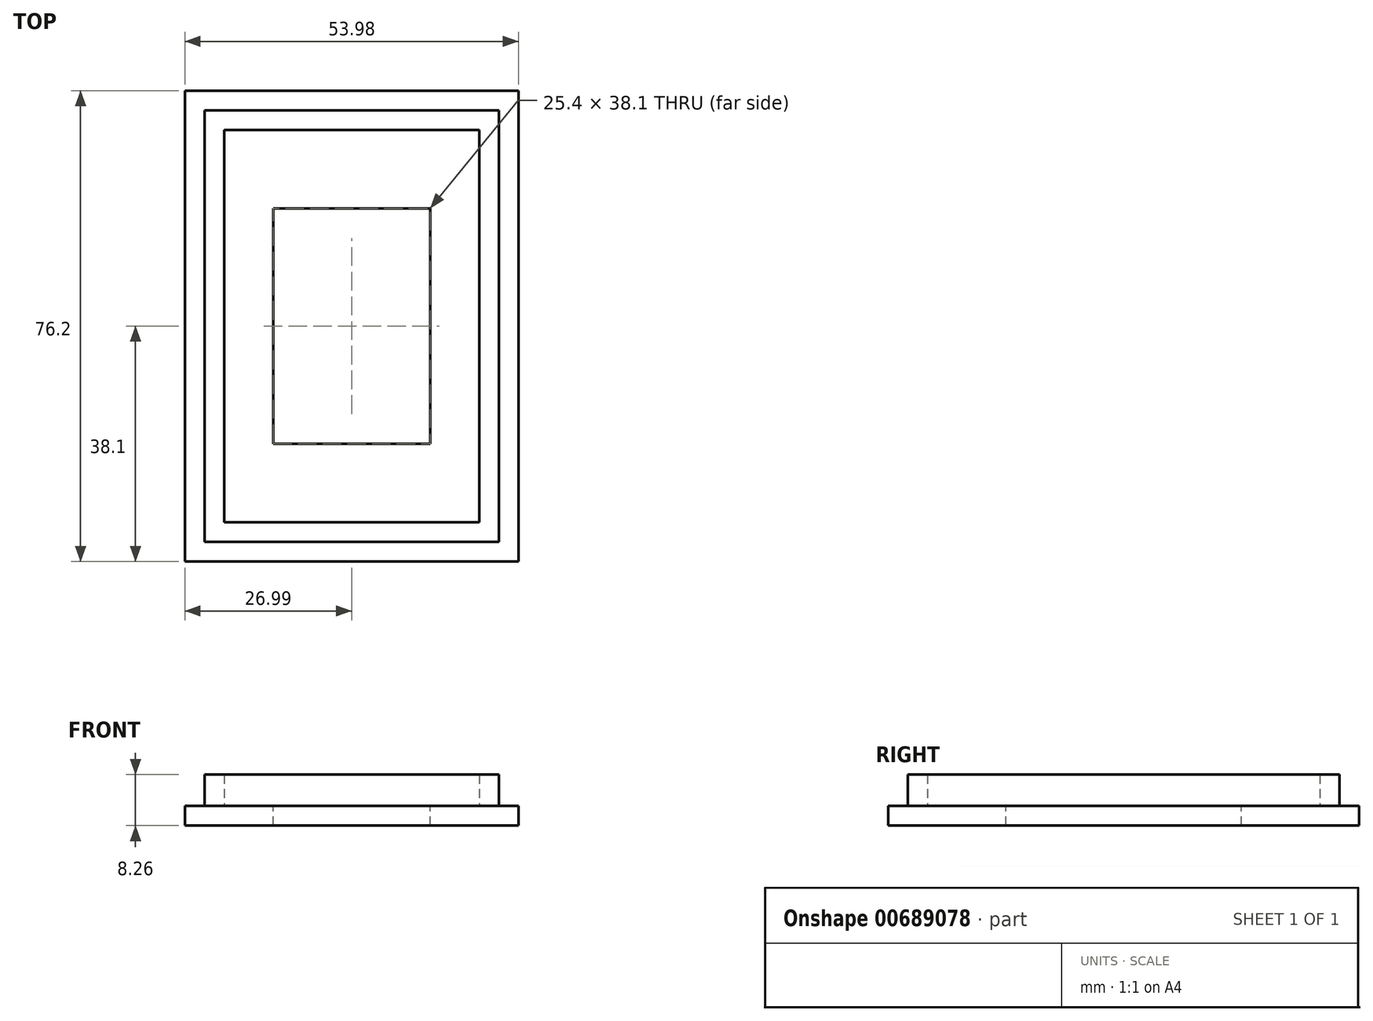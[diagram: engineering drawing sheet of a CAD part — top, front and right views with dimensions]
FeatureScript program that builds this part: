
annotation { "Feature Type Name" : "Feature", "Feature Type Description" : "" }
export const myFeature = defineFeature(function(context is Context, id is Id, definition is map)
    precondition{}
    {
        {
            var Q0;
            Q0=qCreatedBy(makeId("Top.planeOp"),FACE);
            var sketch = newSketch(context, id + "F0", { "sketchPlane" : qUnion([Q0])});
            skLineSegment(sketch, "E0.bottom", {"start": v(-26.99, 38.1) * mm, "end": v(26.99, 38.1) * mm});
            skLineSegment(sketch, "E0.top", {"start": v(-26.99, -38.1) * mm, "end": v(26.99, -38.1) * mm});
            skLineSegment(sketch, "E0.left", {"start": v(-26.99, 38.1) * mm, "end": v(-26.99, -38.1) * mm});
            skLineSegment(sketch, "E0.right", {"start": v(26.99, 38.1) * mm, "end": v(26.99, -38.1) * mm});
            skPoint(sketch, "E0.middle", {"position": v(0, 0) * mm});
            skSolve(sketch);
        }
        {
            var Q0;
            Q0=makeQuery(id+"F0.imprint","IMPRINT",FACE,{"disambiguationData":[TD([[makeQuery(id+"F0.imprint","IMPRINT",EDGE,{"derivedFrom":sQuery(id+"F0.wireOp",EDGE,"E0.bottom")}),-1.0]])]});
            extrude(context, id + "F1", {"entities" : qUnion([Q0]), "depth" : 3.17 * mm, "offsetDistance" : 25.4 * mm});
        }
        {
            var Q0;
            Q0=makeQuery(id+"F1.opExtrude","CAP_FACE",FACE,{"disambiguationData":[OSD([sQuery(id+"F0.wireOp",EDGE,"E0.bottom"),sQuery(id+"F0.wireOp",EDGE,"E0.top"),sQuery(id+"F0.wireOp",EDGE,"E0.left"),sQuery(id+"F0.wireOp",EDGE,"E0.right")])],"isStart":false});
            var sketch = newSketch(context, id + "F2", { "sketchPlane" : qUnion([Q0])});
            skLineSegment(sketch, "E1.bottom", {"start": v(-23.81, 34.93) * mm, "end": v(23.81, 34.93) * mm});
            skLineSegment(sketch, "E1.top", {"start": v(-23.81, -34.93) * mm, "end": v(23.81, -34.93) * mm});
            skLineSegment(sketch, "E1.left", {"start": v(-23.81, 34.93) * mm, "end": v(-23.81, -34.93) * mm});
            skLineSegment(sketch, "E1.right", {"start": v(23.81, 34.93) * mm, "end": v(23.81, -34.93) * mm});
            skPoint(sketch, "E1.middle", {"position": v(0, 0) * mm});
            skSolve(sketch);
        }
        {
            var Q0;
            Q0=makeQuery(id+"F2.imprint","IMPRINT",FACE,{"disambiguationData":[TD([[makeQuery(id+"F2.imprint","IMPRINT",EDGE,{"derivedFrom":sQuery(id+"F2.wireOp",EDGE,"E1.bottom")}),-1.0]])]});
            extrude(context, id + "F3", {"entities" : qUnion([Q0]), "operationType" : NewBodyOperationType.ADD, "depth" : 5.08 * mm, "offsetDistance" : 25.4 * mm});
        }
        {
            var Q0;
            Q0=makeQuery(id+"F3.opExtrude","CAP_FACE",FACE,{"disambiguationData":[OSD([sQuery(id+"F2.wireOp",EDGE,"E1.bottom"),sQuery(id+"F2.wireOp",EDGE,"E1.top"),sQuery(id+"F2.wireOp",EDGE,"E1.left"),sQuery(id+"F2.wireOp",EDGE,"E1.right")])],"isStart":false});
            shell(context, id + "F4", {"entities" : qUnion([Q0]), "thickness" : 3.17 * mm});
        }
        {
            var Q0;
            Q0=makeQuery(id+"F4.opShell","OFFSET_FACE",FACE,{"disambiguationData":[OSD([sQuery(id+"F0.wireOp",EDGE,"E0.bottom"),sQuery(id+"F0.wireOp",EDGE,"E0.top"),sQuery(id+"F0.wireOp",EDGE,"E0.left"),sQuery(id+"F0.wireOp",EDGE,"E0.right")])]});
            var sketch = newSketch(context, id + "F5", { "sketchPlane" : qUnion([Q0])});
            skLineSegment(sketch, "E2.bottom", {"start": v(-12.7, 19.05) * mm, "end": v(12.7, 19.05) * mm});
            skLineSegment(sketch, "E2.top", {"start": v(-12.7, -19.05) * mm, "end": v(12.7, -19.05) * mm});
            skLineSegment(sketch, "E2.left", {"start": v(-12.7, 19.05) * mm, "end": v(-12.7, -19.05) * mm});
            skLineSegment(sketch, "E2.right", {"start": v(12.7, 19.05) * mm, "end": v(12.7, -19.05) * mm});
            skPoint(sketch, "E2.middle", {"position": v(0, 0) * mm});
            skSolve(sketch);
        }
        {
            var Q0;
            Q0=makeQuery(id+"F5.imprint","IMPRINT",FACE,{"disambiguationData":[TD([[makeQuery(id+"F5.imprint","IMPRINT",EDGE,{"derivedFrom":sQuery(id+"F5.wireOp",EDGE,"E2.bottom")}),-1.0]])]});
            extrude(context, id + "F6", {"entities" : qUnion([Q0]), "operationType" : NewBodyOperationType.REMOVE, "oppositeDirection" : true, "depth" : 25.4 * mm, "offsetDistance" : 25.4 * mm});
        }
    });
